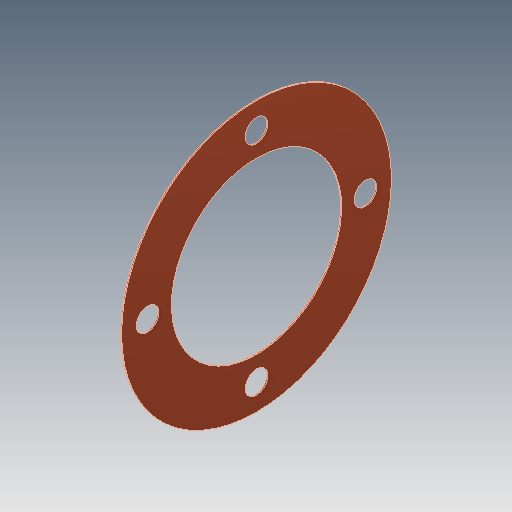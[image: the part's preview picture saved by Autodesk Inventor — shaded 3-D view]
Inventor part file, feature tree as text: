
AUTODESK INVENTOR PART (.ipt)
format: ipt  version: 2025 (Build 290162000, 162)  size: 102,912 bytes
history: native  units: in
note: dims shown in document units (in); Inventor stores cm internally (conversion verified against a paired STEP export)
features: sketch x2, extrude x1
ambient origin geometry x8: Origin, YZ Plane, XZ Plane, XY Plane, X Axis, Y Axis, Z Axis, Center Point
bodies: 实体1 (feature_tree)
feature tree (3):
  extrude  "拉伸1"  Depth=3.2283in
  sketch  "草图1"  dims[d0=0.4331in d2=3.2283in]
  sketch  "草图 - 环形阵列1"  dims[d1=5.1181in d3=3.2283in d4=0.4331in d5=2.0669in d6=1.5748in d8=360.0deg d10=0.0197in d11=0.0in]
